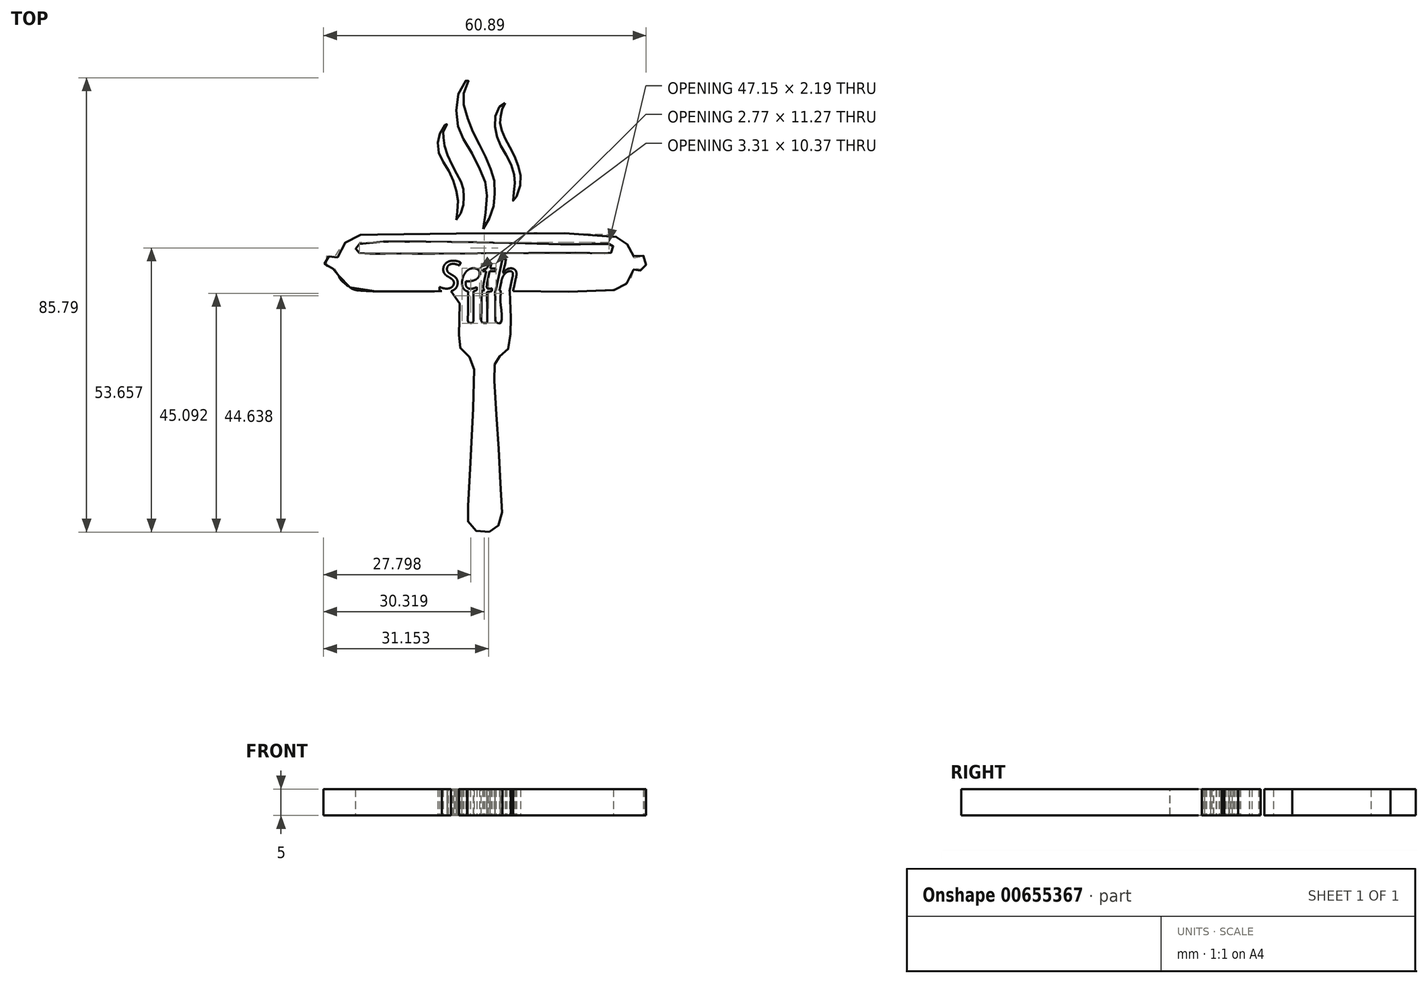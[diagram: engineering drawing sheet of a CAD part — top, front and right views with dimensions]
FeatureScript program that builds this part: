
annotation { "Feature Type Name" : "Feature", "Feature Type Description" : "" }
export const myFeature = defineFeature(function(context is Context, id is Id, definition is map)
    precondition{}
    {
        {
            var Q0;
            Q0=qCreatedBy(makeId("Top.planeOp"),FACE);
            var sketch = newSketch(context, id + "F0", { "sketchPlane" : qUnion([Q0])});
            skFitSpline(sketch, "E0", {"points": [v(0, -44.05) * mm, v(1.6, -43.87) * mm, v(2.36, -43.35) * mm, v(2.88, -42.73) * mm, v(3.45, -41.93) * mm, v(3.5, -39.47) * mm, v(3.07, -31.81) * mm, v(2.55, -23.5) * mm, v(2.03, -15.17) * mm, v(2.03, -12.76) * mm, v(2.2, -12.24) * mm, v(2.39, -11.79) * mm, v(2.79, -11.08) * mm, v(3.6, -10.5) * mm, v(4.26, -10) * mm, v(4.89, -9.07) * mm, v(5.06, -7.42) * mm, v(5.2, -5.36) * mm, v(5.15, -3.13) * mm, v(5.02, 1.55) * mm, v(5.24, 1.55) * mm, v(23.4, 1.55) * mm, v(25.27, 1.86) * mm, v(26.48, 2.49) * mm, v(27.64, 3.6) * mm, v(28.3, 5.16) * mm, v(28.44, 5.88) * mm, v(28.89, 5.34) * mm, v(29.56, 5.25) * mm, v(29.83, 5.61) * mm, v(30.18, 5.66) * mm, v(30.36, 6.01) * mm, v(30.72, 6.5) * mm, v(30.18, 7.3) * mm, v(30.45, 7.84) * mm, v(29.74, 8.2) * mm, v(28.53, 7.57) * mm, v(28.37, 7.86) * mm, v(28.13, 8.98) * mm, v(27.41, 9.97) * mm, v(26.66, 10.8) * mm, v(25.43, 11.44) * mm, v(23.92, 12.04) * mm, v(-20.7, 12.1) * mm, v(-21.04, 12.1) * mm, v(-23.31, 12.07) * mm, v(-24.85, 11.5) * mm, v(-26.62, 10.17) * mm, v(-27.4, 8.87) * mm, v(-27.76, 7.4) * mm, v(-28.7, 8.3) * mm, v(-29.26, 7.93) * mm, v(-29.6, 8.06) * mm, v(-30.17, 7) * mm, v(-29.66, 6.2) * mm, v(-29.06, 5.06) * mm, v(-27.9, 5.96) * mm, v(-27.36, 5.02) * mm, v(-27.3, 4.29) * mm, v(-26.42, 3.12) * mm, v(-25.02, 2.08) * mm, v(-23.35, 1.55) * mm, v(-4.66, 1.41) * mm, v(-4.47, 1.22) * mm, v(-4.6, -5.77) * mm, v(-4.6, -7.88) * mm, v(-4.47, -9.06) * mm, v(-3.83, -9.9) * mm, v(-2.87, -10.83) * mm, v(-2.2, -11.33) * mm, v(-1.81, -12.38) * mm, v(-2.07, -23.63) * mm, v(-2.93, -39.7) * mm, v(-3.04, -41.43) * mm, v(-2.74, -42.44) * mm, v(-1.94, -43.4) * mm, v(-1.14, -43.91) * mm, v(0, -44.05) * mm]});
            skFitSpline(sketch, "E1", {"points": [v(-2.14, -4.55) * mm, v(-1.86, -4.26) * mm, v(-1.84, -3.98) * mm, v(-1.86, -0.26) * mm, v(-1.84, 1.5) * mm, v(-1.84, 1.54) * mm, v(-2.82, 1.54) * mm, v(-2.84, 1.38) * mm, v(-2.85, 1.24) * mm, v(-2.92, -2.88) * mm, v(-2.88, -4.31) * mm, v(-2.5, -4.58) * mm, v(-2.14, -4.55) * mm]});
            skFitSpline(sketch, "E2", {"points": [v(0.66, 1.54) * mm, v(-0.25, 1.56) * mm, v(-0.28, 1.54) * mm, v(-0.38, -3.2) * mm, v(-0.33, -4.3) * mm, v(0.13, -4.58) * mm, v(0.6, -4.55) * mm, v(0.71, -4.36) * mm, v(0.7, -0.3) * mm, v(0.66, 1.12) * mm, v(0.7, 1.29) * mm, v(0.66, 1.54) * mm]});
            skFitSpline(sketch, "E3", {"points": [v(3.25, -4.53) * mm, v(3.24, -0.86) * mm, v(3.24, 0.72) * mm, v(3.25, 1.53) * mm, v(3.2, 1.54) * mm, v(2.32, 1.5) * mm, v(2.23, 0.83) * mm, v(2.27, -3.85) * mm, v(2.5, -4.47) * mm, v(3.25, -4.53) * mm]});
            skFitSpline(sketch, "E4", {"points": [v(-23.43, 10.37) * mm, v(11.94, 10.37) * mm, v(19.93, 10.33) * mm, v(21.83, 10.35) * mm, v(23.5, 10.35) * mm, v(23.92, 10.35) * mm, v(24.35, 10.16) * mm, v(24.54, 9.28) * mm, v(23.92, 8.59) * mm, v(23.21, 8.59) * mm, v(-11.11, 8.52) * mm, v(-15.4, 8.56) * mm, v(-20.56, 8.5) * mm, v(-23.3, 8.65) * mm, v(-24.1, 9.08) * mm, v(-24.01, 9.78) * mm, v(-23.43, 10.37) * mm]});
            skFitSpline(sketch, "E5", {"points": [v(0, 13.19) * mm, v(0.8, 14.56) * mm, v(1.7, 16.5) * mm, v(2.08, 18.62) * mm, v(2.17, 20.37) * mm, v(2.03, 22.36) * mm, v(1.56, 24.1) * mm, v(0.7, 26.14) * mm, v(0, 27.75) * mm, v(-1.37, 30.25) * mm, v(-2.32, 32.38) * mm, v(-3.21, 34.74) * mm, v(-3.73, 36.92) * mm, v(-3.7, 38.47) * mm, v(-3.38, 40.25) * mm, v(-2.45, 41.72) * mm, v(-3.38, 41.14) * mm, v(-4.72, 38.73) * mm, v(-5.12, 35.34) * mm, v(-4.72, 32.44) * mm, v(-3.83, 30.35) * mm, v(-2.1, 27.4) * mm, v(-0.53, 24.1) * mm, v(0.36, 22) * mm, v(0.63, 19.86) * mm, v(0.5, 16.65) * mm, v(0, 13.19) * mm]});
            skFitSpline(sketch, "E6", {"points": [v(-5.12, 14.9) * mm, v(-4.14, 16.43) * mm, v(-3.74, 18.08) * mm, v(-3.7, 19.82) * mm, v(-3.88, 21.24) * mm, v(-4.63, 22.9) * mm, v(-5.88, 25.21) * mm, v(-7, 27.76) * mm, v(-7.49, 29.9) * mm, v(-7.58, 31.06) * mm, v(-7.44, 31.86) * mm, v(-6.78, 33.29) * mm, v(-7.71, 32.22) * mm, v(-8.52, 30.03) * mm, v(-8.38, 27.53) * mm, v(-7.09, 25.08) * mm, v(-5.7, 22.4) * mm, v(-4.95, 19.68) * mm, v(-4.81, 17) * mm, v(-5.12, 14.9) * mm]});
            skFitSpline(sketch, "E7", {"points": [v(4.11, 36.95) * mm, v(3.58, 35.88) * mm, v(3.3, 34.67) * mm, v(3.17, 33.42) * mm, v(3.4, 32.1) * mm, v(4.12, 30.26) * mm, v(5.28, 28.03) * mm, v(6.44, 25.53) * mm, v(7.02, 23.08) * mm, v(6.67, 20.36) * mm, v(5.69, 18.44) * mm, v(5.69, 19.47) * mm, v(5.9, 21.7) * mm, v(5.77, 23.57) * mm, v(4.84, 26.3) * mm, v(3.28, 28.88) * mm, v(2.43, 31.2) * mm, v(2.16, 34.01) * mm, v(3.19, 36.42) * mm, v(4.11, 36.95) * mm]});
            skText(sketch, "E8", { "text": "Seth", "fontName": "OpenSans-Italic.ttf"});
            const initialGuessF0  = {"E8": [-0.00841, 0.00143, 1, 0, 0.00574]};
            skSetInitialGuess(sketch, initialGuessF0);
            skSolve(sketch);
        }
        {
            var Q0;
            Q0=makeQuery(id+"F0.imprint","IMPRINT",FACE,{"disambiguationData":[TD([[makeQuery(id+"F0.imprint","IMPRINT",EDGE,{"derivedFrom":sQuery(id+"F0.wireOp",EDGE,"E5")}),1.0]])]});
            var Q1;
            Q1=makeQuery(id+"F0.imprint","IMPRINT",FACE,{"disambiguationData":[TD([[makeQuery(id+"F0.imprint","IMPRINT",EDGE,{"derivedFrom":sQuery(id+"F0.wireOp",EDGE,"E6")}),1.0]])]});
            var Q2;
            Q2=makeQuery(id+"F0.imprint","IMPRINT",FACE,{"disambiguationData":[TD([[makeQuery(id+"F0.imprint","IMPRINT",EDGE,{"derivedFrom":sQuery(id+"F0.wireOp",EDGE,"E7")}),-1.0]])]});
            var Q3;
            Q3=makeQuery(id+"F0.imprint","IMPRINT",FACE,{"disambiguationData":[TD([[makeQuery(id+"F0.imprint","IMPRINT",EDGE,{"derivedFrom":sQuery(id+"F0.wireOp",EDGE,"E0")}),1.0]])]});
            extrude(context, id + "F1", {"entities" : qUnion([Q0, Q1, Q2, Q3]), "depth" : 5 * mm, "offsetDistance" : 25 * mm});
        }
    });
